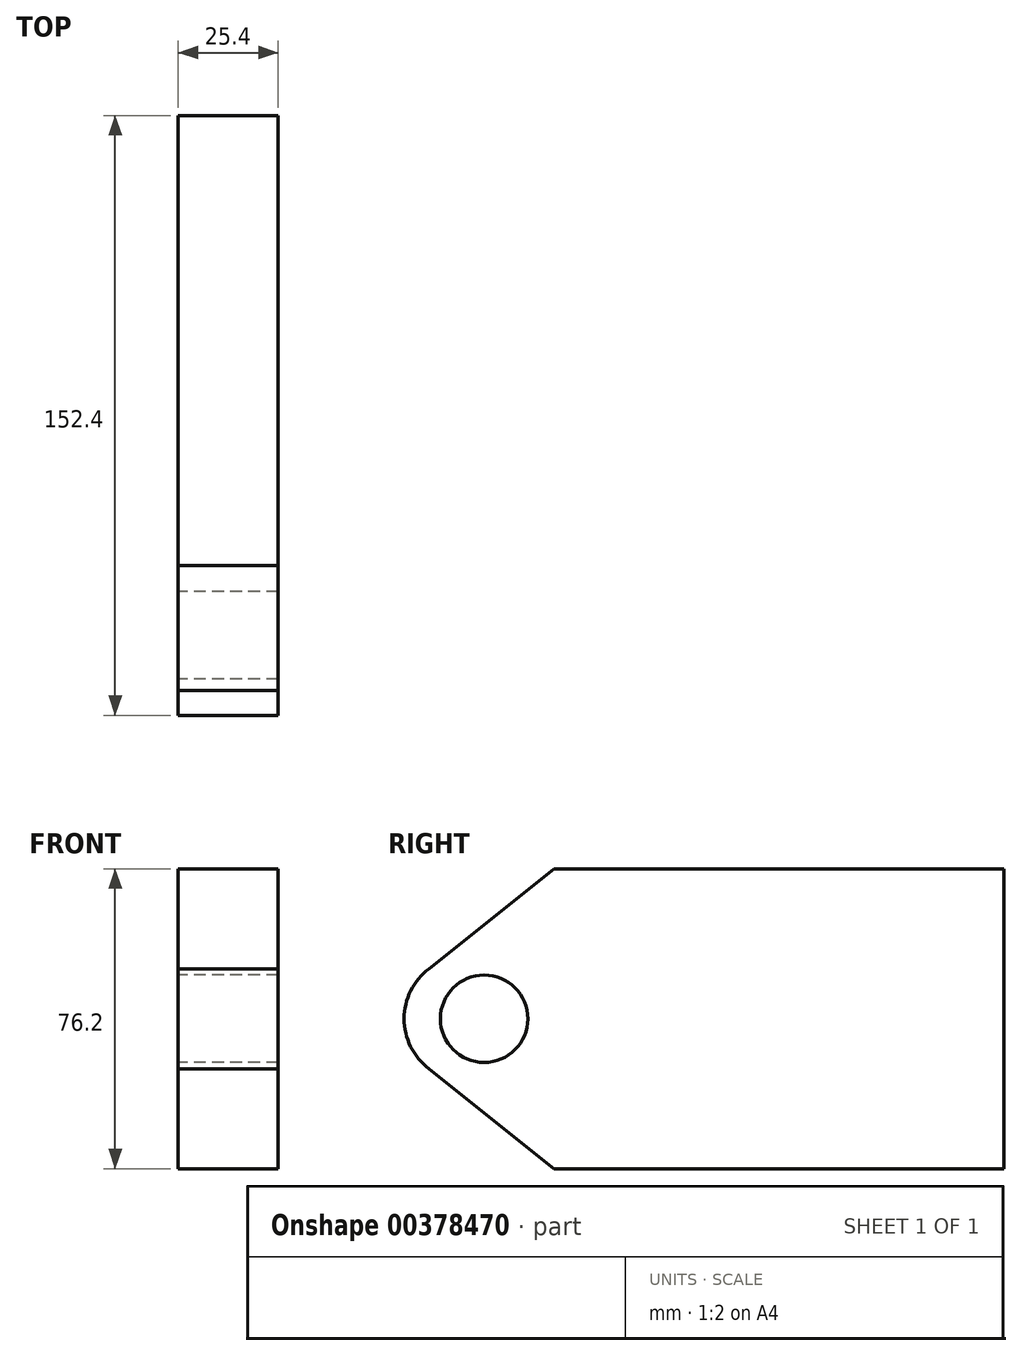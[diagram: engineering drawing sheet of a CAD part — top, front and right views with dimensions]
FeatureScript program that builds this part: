
annotation { "Feature Type Name" : "Feature", "Feature Type Description" : "" }
export const myFeature = defineFeature(function(context is Context, id is Id, definition is map)
    precondition{}
    {
        {
            var Q0;
            Q0=qCreatedBy(makeId("Right.planeOp"),FACE);
            var sketch = newSketch(context, id + "F0", { "sketchPlane" : qUnion([Q0])});
            skLineSegment(sketch, "E0.bottom", {"start": v(-38.1, 38.1) * mm, "end": v(76.2, 38.1) * mm});
            skLineSegment(sketch, "E0.top", {"start": v(-38.1, -38.1) * mm, "end": v(76.2, -38.1) * mm});
            skLineSegment(sketch, "E0.right", {"start": v(76.2, 38.1) * mm, "end": v(76.2, -38.1) * mm});
            skPoint(sketch, "E0.middle", {"position": v(0, 0) * mm});
            skArc(sketch, "E1", {"start": v(-69.85, 12.7) * mm, "mid": v(-76.2, 0) * mm, "end": v(-69.85, -12.7) * mm});
            skLineSegment(sketch, "E2", {"start": v(-69.85, 12.7) * mm, "end": v(-38.1, 38.1) * mm});
            skLineSegment(sketch, "E3", {"start": v(-69.85, -12.7) * mm, "end": v(-38.1, -38.1) * mm});
            skPoint(sketch, "E4.orphan", {"position": v(-76.2, 38.1) * mm});
            skPoint(sketch, "E5.orphan", {"position": v(-76.2, -38.1) * mm});
            skCircle(sketch, "E6", {"center": v(-55.88, 0) * mm, "radius": 11.11 * mm});
            skSolve(sketch);
        }
        {
            var Q0;
            Q0 = qSketchRegion(id + "F0", true);
            extrude(context, id + "F1", {"entities" : qUnion([Q0]), "depth" : 25.4 * mm});
        }
    });
